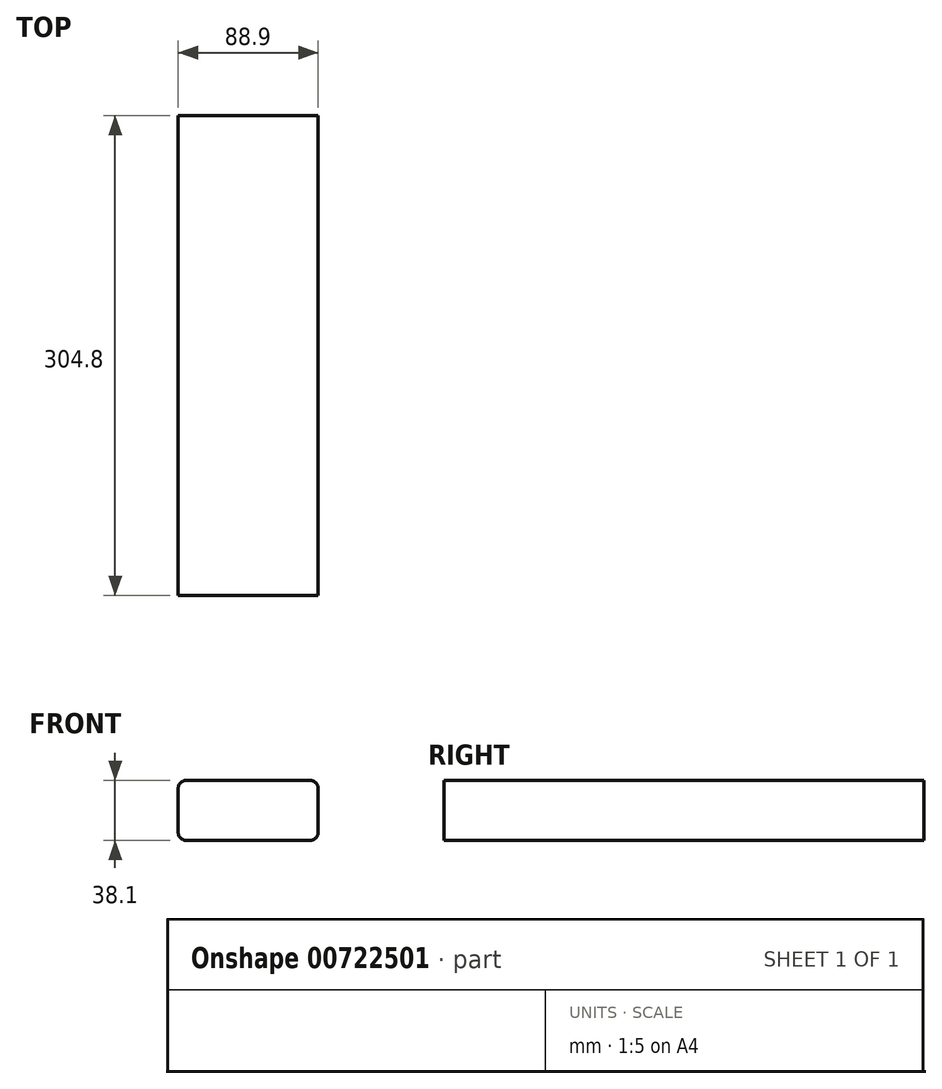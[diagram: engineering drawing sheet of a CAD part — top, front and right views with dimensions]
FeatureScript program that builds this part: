
annotation { "Feature Type Name" : "Feature", "Feature Type Description" : "" }
export const myFeature = defineFeature(function(context is Context, id is Id, definition is map)
    precondition{}
    {
        {
            var Q0;
            Q0=qCreatedBy(makeId("Top.planeOp"),FACE);
            var sketch = newSketch(context, id + "F0", { "sketchPlane" : qUnion([Q0])});
            skLineSegment(sketch, "E0", {"start": v(0, 0) * mm, "end": v(0, -304.8) * mm});
            skLineSegment(sketch, "E1", {"start": v(0, -304.8) * mm, "end": v(88.9, -304.8) * mm});
            skLineSegment(sketch, "E2", {"start": v(88.9, -304.8) * mm, "end": v(88.9, 0) * mm});
            skLineSegment(sketch, "E3", {"start": v(88.9, 0) * mm, "end": v(0, 0) * mm});
            skSolve(sketch);
        }
        {
            var Q0;
            Q0=makeQuery(id+"F0.imprint","IMPRINT",FACE,{"disambiguationData":[TD([[makeQuery(id+"F0.imprint","IMPRINT",EDGE,{"derivedFrom":sQuery(id+"F0.wireOp",EDGE,"E0")}),1.0]])]});
            extrude(context, id + "F1", {"entities" : qUnion([Q0]), "depth" : 38.1 * mm, "offsetDistance" : 25.4 * mm});
        }
        {
            var Q0;
            Q0=makeQuery(id+"F1.opExtrude","CAP_EDGE",EDGE,{"disambiguationData":[OSD([sQuery(id+"F0.wireOp",EDGE,"E0")])],"isStart":false});
            var Q1;
            Q1=makeQuery(id+"F1.opExtrude","CAP_EDGE",EDGE,{"disambiguationData":[OSD([sQuery(id+"F0.wireOp",EDGE,"QFeDoF2F-YcUx-ajFQ-dHWQ-Pq5UQB8hivIF")])],"isStart":false});
            var Q2;
            Q2=makeQuery(id+"F1.opExtrude","CAP_EDGE",EDGE,{"disambiguationData":[OSD([sQuery(id+"F0.wireOp",EDGE,"QFeDoF2F-YcUx-ajFQ-dHWQ-Pq5UQB8hivIF")])],"isStart":true});
            var Q3;
            Q3=makeQuery(id+"F1.opExtrude","CAP_EDGE",EDGE,{"disambiguationData":[OSD([sQuery(id+"F0.wireOp",EDGE,"E0")])],"isStart":true});
            fillet(context, id + "F2", {"entities" : qUnion([Q0, Q1, Q2, Q3]), "radius" : 5.08 * mm, "tangentPropagation" : true, "allowEdgeOverflow" : false});
        }
        {
            var Q0;
            Q0=makeQuery(id+"F1.opExtrude","CAP_EDGE",EDGE,{"disambiguationData":[OSD([sQuery(id+"F0.wireOp",EDGE,"E2")])],"isStart":false});
            var Q1;
            Q1=makeQuery(id+"F1.opExtrude","CAP_EDGE",EDGE,{"disambiguationData":[OSD([sQuery(id+"F0.wireOp",EDGE,"E2")])],"isStart":true});
            fillet(context, id + "F3", {"entities" : qUnion([Q0, Q1]), "radius" : 5.08 * mm, "tangentPropagation" : true, "allowEdgeOverflow" : false});
        }
    });
